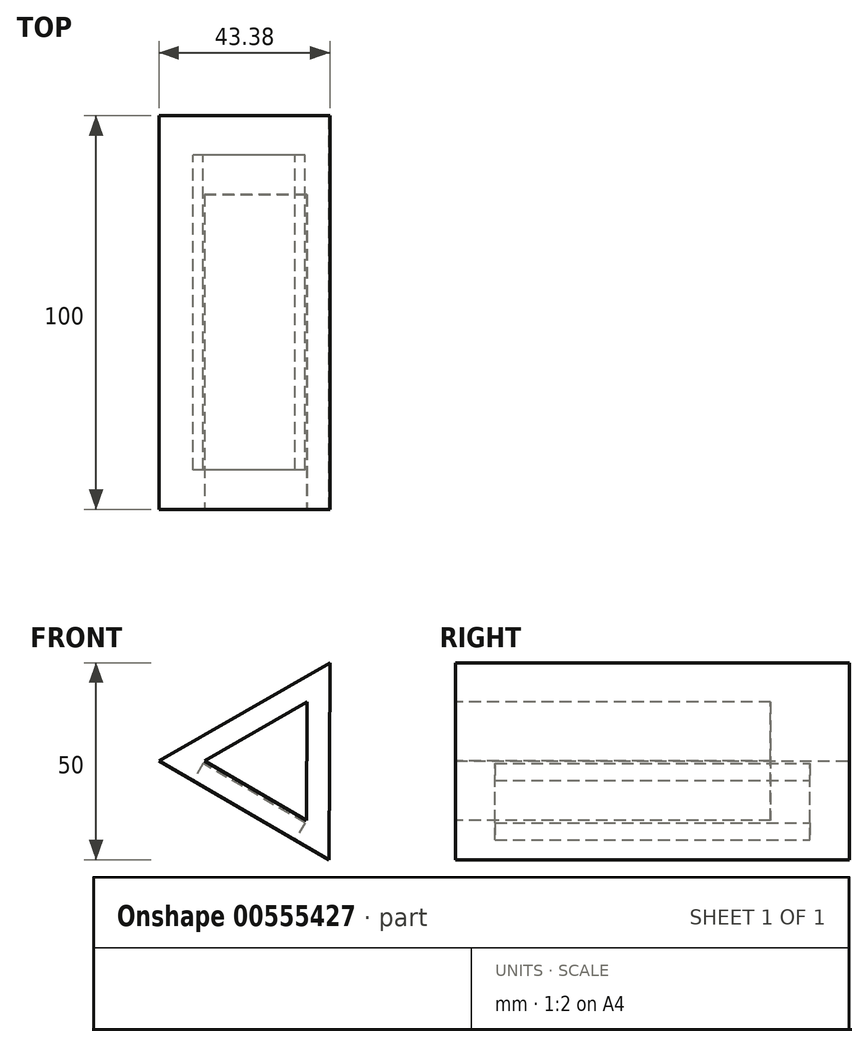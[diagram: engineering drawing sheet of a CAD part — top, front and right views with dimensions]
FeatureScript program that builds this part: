
annotation { "Feature Type Name" : "Feature", "Feature Type Description" : "" }
export const myFeature = defineFeature(function(context is Context, id is Id, definition is map)
    precondition{}
    {
        {
            var Q0;
            Q0=qCreatedBy(makeId("Front.planeOp"),FACE);
            var sketch = newSketch(context, id + "F0", { "sketchPlane" : qUnion([Q0])});
            skCircle(sketch, "E0.cCircle", {"center": v(0, 0) * mm, "radius": 14.43 * mm, "construction": true});
            skLineSegment(sketch, "E0.0", {"start": v(-28.87, 0.1) * mm, "end": v(14.51, 24.95) * mm});
            skLineSegment(sketch, "E0.1", {"start": v(14.51, 24.95) * mm, "end": v(14.35, -25.05) * mm});
            skLineSegment(sketch, "E0.2", {"start": v(14.35, -25.05) * mm, "end": v(-28.87, 0.1) * mm});
            skPoint(sketch, "E0.0.midPoint", {"position": v(-7.18, 12.52) * mm});
            skSolve(sketch);
        }
        {
            var Q0;
            Q0 = qSketchRegion(id + "F0", true);
            extrude(context, id + "F1", {"entities" : qUnion([Q0]), "depth" : 100 * mm, "offsetDistance" : 25 * mm});
        }
        {
            var Q0;
            Q0=makeQuery(id+"F1.opExtrude","SWEPT_FACE",FACE,{"disambiguationData":[OSD([sQuery(id+"F0.wireOp",EDGE,"E0.2")])]});
            var sketch = newSketch(context, id + "F2", { "sketchPlane" : qUnion([Q0])});
            skLineSegment(sketch, "E1.bottom", {"start": v(15, 90) * mm, "end": v(-15, 90) * mm});
            skLineSegment(sketch, "E1.top", {"start": v(15, 10) * mm, "end": v(-15, 10) * mm});
            skLineSegment(sketch, "E1.left", {"start": v(15, 90) * mm, "end": v(15, 10) * mm});
            skLineSegment(sketch, "E1.right", {"start": v(-15, 90) * mm, "end": v(-15, 10) * mm});
            skPoint(sketch, "E1.middle", {"position": v(0, 50) * mm});
            skPoint(sketch, "E1.middle.positionSnap0", {"position": v(25, 50) * mm});
            skPoint(sketch, "E1.centerSnap0", {"position": v(25, 50) * mm});
            skSolve(sketch);
        }
        {
            var Q0;
            Q0 = qSketchRegion(id + "F2", true);
            extrude(context, id + "F3", {"entities" : qUnion([Q0]), "operationType" : NewBodyOperationType.REMOVE, "oppositeDirection" : true, "depth" : 5 * mm, "offsetDistance" : 25 * mm});
        }
        {
            var Q0;
            Q0=makeQuery(id+"F1.opExtrude","CAP_FACE",FACE,{"disambiguationData":[OSD([sQuery(id+"F0.wireOp",EDGE,"E0.0"),sQuery(id+"F0.wireOp",EDGE,"E0.1"),sQuery(id+"F0.wireOp",EDGE,"E0.2")])],"isStart":false});
            var sketch = newSketch(context, id + "F4", { "sketchPlane" : qUnion([Q0])});
            skCircle(sketch, "E2.cCircle", {"center": v(0, 0) * mm, "radius": 8.66 * mm, "construction": true});
            skLineSegment(sketch, "E2.0", {"start": v(-17.32, 0.06) * mm, "end": v(8.7, 14.97) * mm});
            skLineSegment(sketch, "E2.1", {"start": v(8.7, 14.97) * mm, "end": v(8.61, -15.03) * mm});
            skLineSegment(sketch, "E2.2", {"start": v(8.61, -15.03) * mm, "end": v(-17.32, 0.06) * mm});
            skPoint(sketch, "E2.0.midPoint", {"position": v(-4.3, 7.51) * mm});
            skSolve(sketch);
        }
        {
            var Q0;
            Q0=makeQuery(id+"F4.imprint","IMPRINT",FACE,{"disambiguationData":[TD([[makeQuery(id+"F4.imprint","IMPRINT",EDGE,{"derivedFrom":sQuery(id+"F4.wireOp",EDGE,"E2.0")}),-1.0]])]});
            extrude(context, id + "F5", {"entities" : qUnion([Q0]), "operationType" : NewBodyOperationType.REMOVE, "oppositeDirection" : true, "depth" : 80 * mm, "offsetDistance" : 25 * mm});
        }
    });
